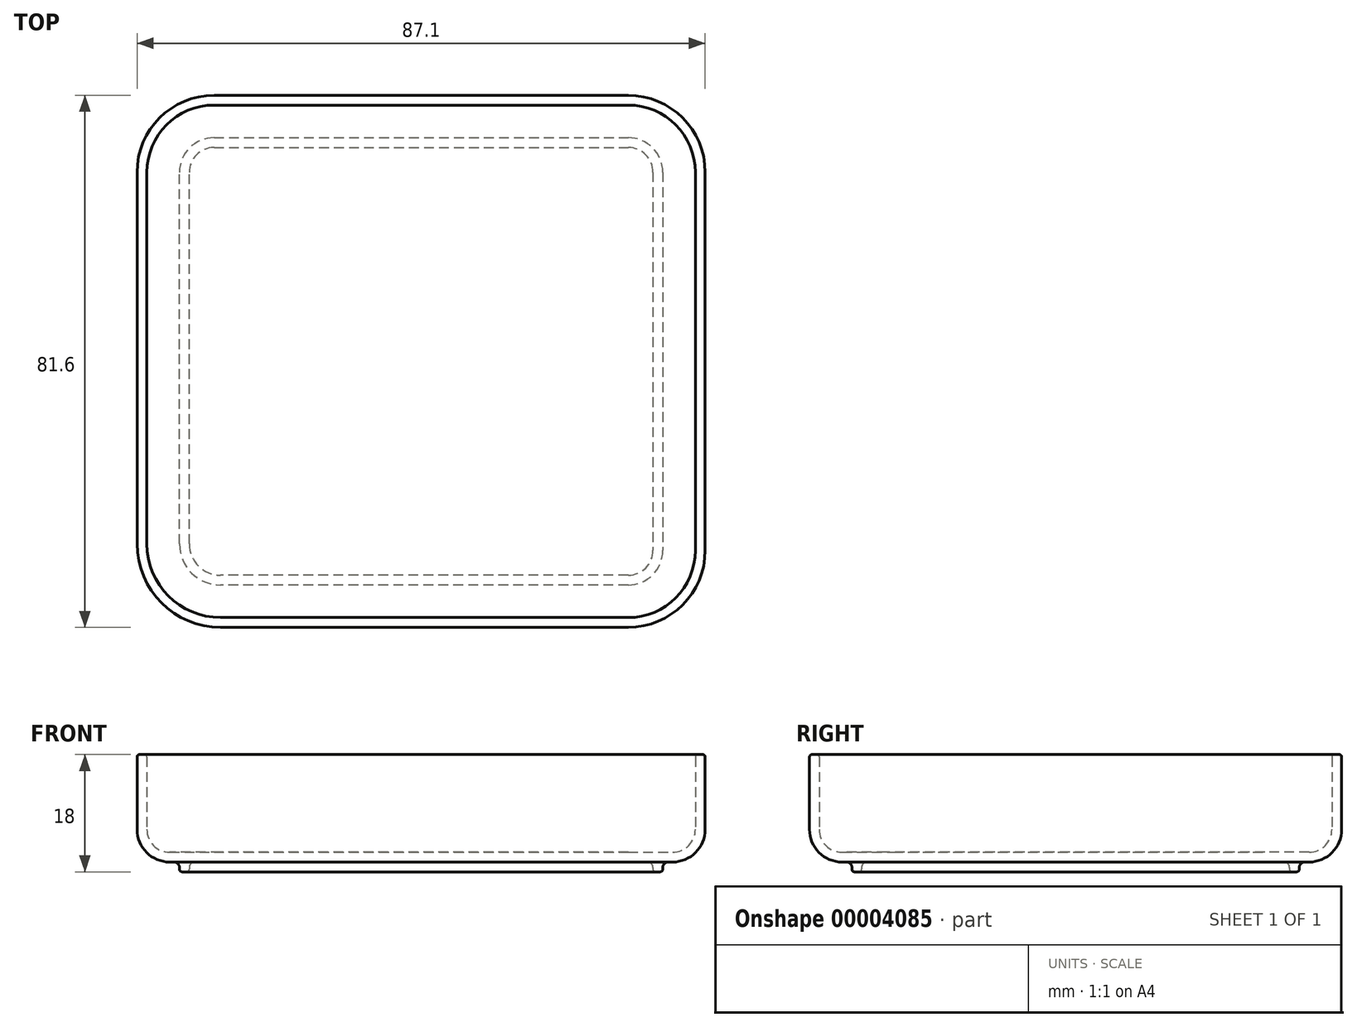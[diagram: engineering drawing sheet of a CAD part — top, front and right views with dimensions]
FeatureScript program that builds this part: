
annotation { "Feature Type Name" : "Feature", "Feature Type Description" : "" }
export const myFeature = defineFeature(function(context is Context, id is Id, definition is map)
    precondition{}
    {
        {
            var Q0;
            Q0=qCreatedBy(makeId("Top.planeOp"),FACE);
            var sketch = newSketch(context, id + "F0", { "sketchPlane" : qUnion([Q0])});
            skLineSegment(sketch, "E0.rect.bottom", {"start": v(-31.5, 32) * mm, "end": v(32, 32) * mm});
            skLineSegment(sketch, "E0.rect.top", {"start": v(-30.5, -32) * mm, "end": v(32, -32) * mm});
            skLineSegment(sketch, "E0.rect.left", {"start": v(-34.5, 29) * mm, "end": v(-34.5, -28) * mm});
            skPoint(sketch, "E0.rect.middle", {"position": v(0, 0) * mm});
            skPoint(sketch, "E1.visualSharp", {"position": v(-34.5, 32) * mm});
            skArc(sketch, "E1.filletArc", {"start": v(-31.5, 32) * mm, "mid": v(-33.62, 31.12) * mm, "end": v(-34.5, 29) * mm});
            skPoint(sketch, "E2.visualSharp", {"position": v(34.5, 32) * mm});
            skArc(sketch, "E2.filletArc", {"start": v(35, 29) * mm, "mid": v(34.12, 31.12) * mm, "end": v(32, 32) * mm});
            skPoint(sketch, "E3.visualSharp", {"position": v(34.5, -32) * mm});
            skArc(sketch, "E3.filletArc", {"start": v(32, -32) * mm, "mid": v(34.12, -31.12) * mm, "end": v(35, -29) * mm});
            skPoint(sketch, "E4.visualSharp", {"position": v(-34.5, -32) * mm});
            skArc(sketch, "E4.filletArc", {"start": v(-34.5, -28) * mm, "mid": v(-33.33, -30.83) * mm, "end": v(-30.5, -32) * mm});
            skPoint(sketch, "E5", {"position": v(35, 0) * mm});
            skLineSegment(sketch, "E6", {"start": v(35, 0) * mm, "end": v(35, 29) * mm});
            skLineSegment(sketch, "E7", {"start": v(35, 0) * mm, "end": v(35, -29) * mm});
            skSolve(sketch);
        }
        {
            var Q0;
            Q0=makeQuery(id+"F0.imprint","IMPRINT",FACE,{"disambiguationData":[TD([[makeQuery(id+"F0.imprint","IMPRINT",EDGE,{"derivedFrom":sQuery(id+"F0.wireOp",EDGE,"E0.rect.bottom")}),-1.0]])]});
            extrude(context, id + "F1", {"entities" : qUnion([Q0]), "oppositeDirection" : true, "depth" : 1.5 * mm});
        }
        {
            var Q0;
            Q0=qCreatedBy(makeId("Front.planeOp"),FACE);
            var sketch = newSketch(context, id + "F2", { "sketchPlane" : qUnion([Q0])});
            skLineSegment(sketch, "E8", {"start": v(36.2, -3) * mm, "end": v(36.9, -3) * mm});
            skLineSegment(sketch, "E9", {"start": v(37.3, -2.6) * mm, "end": v(37.3, -2.3) * mm});
            skLineSegment(sketch, "E10", {"start": v(38.1, -1.5) * mm, "end": v(38.8, -1.5) * mm});
            skArc(sketch, "E11", {"start": v(38.8, -1.5) * mm, "mid": v(42.34, -0.04) * mm, "end": v(43.8, 3.5) * mm});
            skLineSegment(sketch, "E12", {"start": v(43.8, 3.5) * mm, "end": v(43.8, 14.6) * mm});
            skLineSegment(sketch, "E13", {"start": v(43.4, 15) * mm, "end": v(42.7, 15) * mm});
            skLineSegment(sketch, "E14", {"start": v(42.3, 14.6) * mm, "end": v(42.3, 3.5) * mm});
            skArc(sketch, "E15", {"start": v(38.8, 0) * mm, "mid": v(41.27, 1.03) * mm, "end": v(42.3, 3.5) * mm});
            skLineSegment(sketch, "E16", {"start": v(38.8, 0) * mm, "end": v(35, 0) * mm});
            skArc(sketch, "E17", {"start": v(35.8, -2.3) * mm, "mid": v(35.57, -1.73) * mm, "end": v(35, -1.5) * mm});
            skLineSegment(sketch, "E18", {"start": v(35.8, -2.3) * mm, "end": v(35.8, -2.6) * mm});
            skPoint(sketch, "E19", {"position": v(35.8, -1.5) * mm});
            skPoint(sketch, "E20.visualSharp", {"position": v(37.3, -1.5) * mm});
            skArc(sketch, "E20.filletArc", {"start": v(38.1, -1.5) * mm, "mid": v(37.53, -1.73) * mm, "end": v(37.3, -2.3) * mm});
            skPoint(sketch, "E21.visualSharp", {"position": v(37.3, -3) * mm});
            skArc(sketch, "E21.filletArc", {"start": v(36.9, -3) * mm, "mid": v(37.18, -2.88) * mm, "end": v(37.3, -2.6) * mm});
            skPoint(sketch, "E22.visualSharp", {"position": v(35.8, -3) * mm});
            skArc(sketch, "E22.filletArc", {"start": v(35.8, -2.6) * mm, "mid": v(35.92, -2.88) * mm, "end": v(36.2, -3) * mm});
            skPoint(sketch, "E23.visualSharp", {"position": v(42.3, 15) * mm});
            skArc(sketch, "E23.filletArc", {"start": v(42.7, 15) * mm, "mid": v(42.42, 14.88) * mm, "end": v(42.3, 14.6) * mm});
            skPoint(sketch, "E24.visualSharp", {"position": v(43.8, 15) * mm});
            skArc(sketch, "E24.filletArc", {"start": v(43.8, 14.6) * mm, "mid": v(43.68, 14.88) * mm, "end": v(43.4, 15) * mm});
            skLineSegment(sketch, "E25", {"start": v(35, 0) * mm, "end": v(35, -1.5) * mm});
            skSolve(sketch);
        }
        {
            var Q0;
            Q0=makeQuery(id+"F2.imprint","IMPRINT",FACE,{"disambiguationData":[TD([[makeQuery(id+"F2.imprint","IMPRINT",EDGE,{"derivedFrom":sQuery(id+"F2.wireOp",EDGE,"E8")}),1.0]])]});
            var Q1;
            Q1=sQuery(id+"F0.wireOp",EDGE,"E6");
            var Q2;
            Q2=sQuery(id+"F0.wireOp",EDGE,"E2.filletArc");
            var Q3;
            Q3=sQuery(id+"F0.wireOp",EDGE,"E0.rect.bottom");
            var Q4;
            Q4=sQuery(id+"F0.wireOp",EDGE,"E1.filletArc");
            var Q5;
            Q5=sQuery(id+"F0.wireOp",EDGE,"E0.rect.left");
            var Q6;
            Q6=sQuery(id+"F0.wireOp",EDGE,"E4.filletArc");
            var Q7;
            Q7=sQuery(id+"F0.wireOp",EDGE,"E0.rect.top");
            var Q8;
            Q8=sQuery(id+"F0.wireOp",EDGE,"E3.filletArc");
            var Q9;
            Q9=sQuery(id+"F0.wireOp",EDGE,"E7");
            sweep(context, id + "F3", {"operationType" : NewBodyOperationType.ADD, "profiles" : qUnion([Q0]), "path" : qUnion([Q1, Q2, Q3, Q4, Q5, Q6, Q7, Q8, Q9])});
        }
    });
